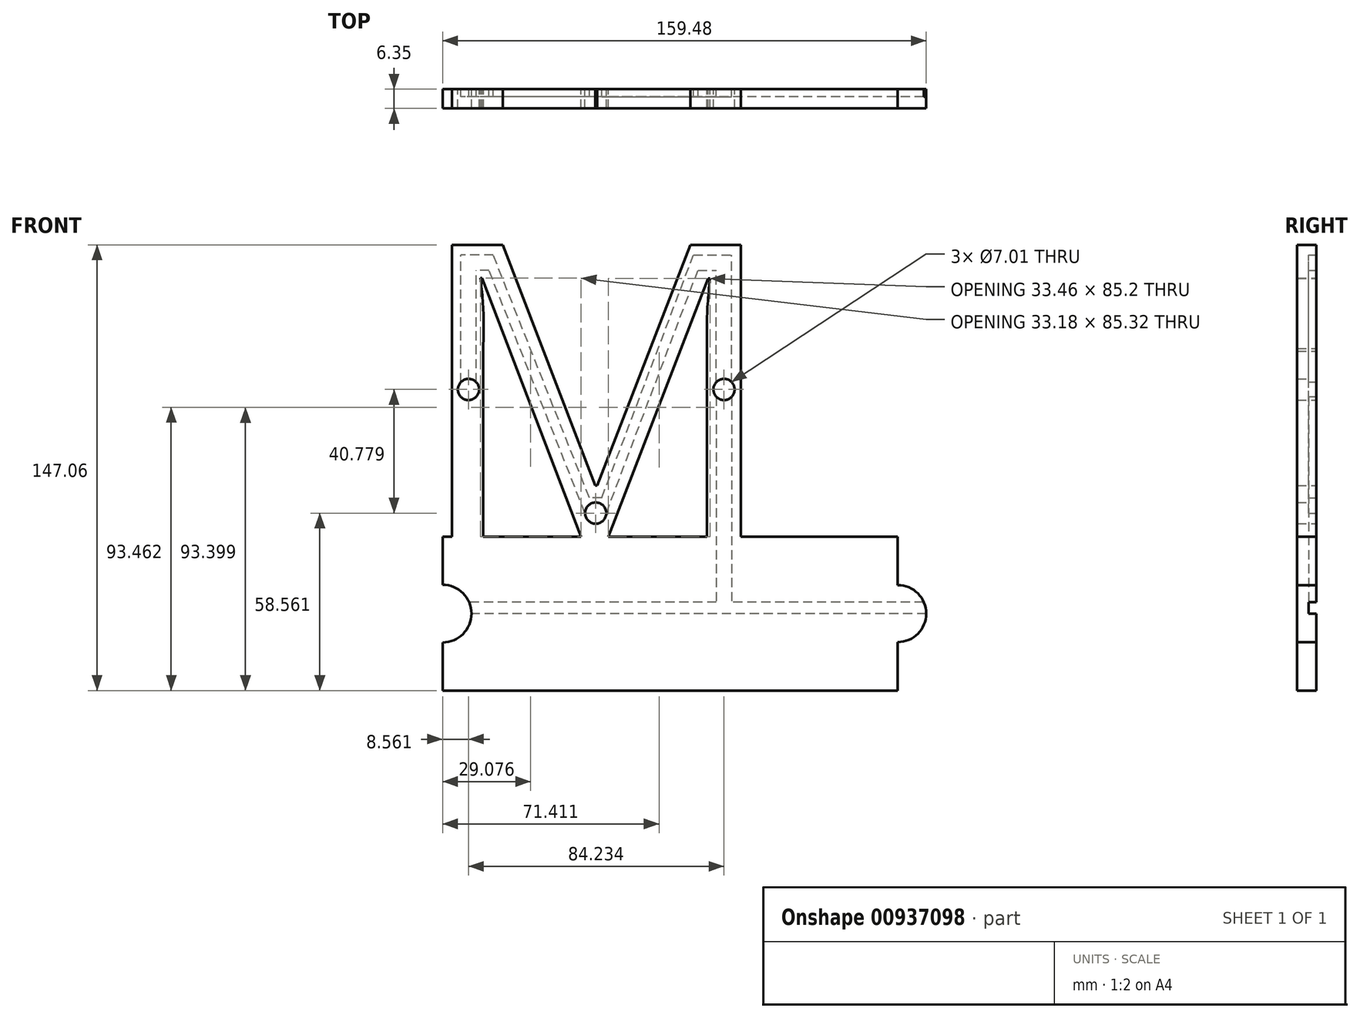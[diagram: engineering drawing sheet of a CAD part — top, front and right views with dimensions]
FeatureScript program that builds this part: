
annotation { "Feature Type Name" : "Feature", "Feature Type Description" : "" }
export const myFeature = defineFeature(function(context is Context, id is Id, definition is map)
    precondition{}
    {
        {
            var Q0;
            Q0=qCreatedBy(makeId("Front.planeOp"),FACE);
            var sketch = newSketch(context, id + "F0", { "sketchPlane" : qUnion([Q0])});
            skText(sketch, "E0", { "text": "M", "fontName": "OpenSans-Regular.ttf"});
            const initialGuessF0  = {"E0": [-0.05865, -0.04854, 1, 0, 0.09708]};
            skSetInitialGuess(sketch, initialGuessF0);
            skSolve(sketch);
        }
        {
            var Q0;
            Q0=qCreatedBy(makeId("Front.planeOp"),FACE);
            var sketch = newSketch(context, id + "F1", { "sketchPlane" : qUnion([Q0])});
            skLineSegment(sketch, "E1.0.0", {"start": v(-2.82, -48.54) * mm, "end": v(6.2, -48.54) * mm});
            skLineSegment(sketch, "E1.0.1", {"start": v(6.2, -48.54) * mm, "end": v(39.12, 36.66) * mm});
            skLineSegment(sketch, "E1.0.2", {"start": v(39.12, 36.66) * mm, "end": v(39.65, 36.66) * mm});
            skFitSpline(sketch, "E1.0.3", {"points": [v(39.65, 36.66) * mm, v(38.72, 24.14) * mm, v(38.72, 13.48) * mm]});
            skLineSegment(sketch, "E1.0.4", {"start": v(38.72, 13.48) * mm, "end": v(38.72, -48.54) * mm});
            skLineSegment(sketch, "E1.0.5", {"start": v(38.72, -48.54) * mm, "end": v(49.9, -48.54) * mm});
            skLineSegment(sketch, "E1.0.6", {"start": v(49.9, -48.54) * mm, "end": v(49.9, 47.72) * mm});
            skLineSegment(sketch, "E1.0.7", {"start": v(49.9, 47.72) * mm, "end": v(33.18, 47.72) * mm});
            skLineSegment(sketch, "E1.0.8", {"start": v(33.18, 47.72) * mm, "end": v(2.44, -31.69) * mm});
            skLineSegment(sketch, "E1.0.9", {"start": v(2.44, -31.69) * mm, "end": v(1.92, -31.69) * mm});
            skLineSegment(sketch, "E1.0.10", {"start": v(1.92, -31.69) * mm, "end": v(-28.57, 47.72) * mm});
            skLineSegment(sketch, "E1.0.11", {"start": v(-28.57, 47.72) * mm, "end": v(-45.42, 47.72) * mm});
            skLineSegment(sketch, "E1.0.12", {"start": v(-45.42, 47.72) * mm, "end": v(-45.42, -48.54) * mm});
            skLineSegment(sketch, "E1.0.13", {"start": v(-45.42, -48.54) * mm, "end": v(-35.08, -48.54) * mm});
            skLineSegment(sketch, "E1.0.14", {"start": v(-35.08, -48.54) * mm, "end": v(-35.08, 12.68) * mm});
            skFitSpline(sketch, "E1.0.15", {"points": [v(-35.08, 12.68) * mm, v(-35.08, 26.65) * mm, v(-36, 36.78) * mm]});
            skLineSegment(sketch, "E1.0.16", {"start": v(-36, 36.78) * mm, "end": v(-35.48, 36.78) * mm});
            skLineSegment(sketch, "E1.0.17", {"start": v(-35.48, 36.78) * mm, "end": v(-2.82, -48.54) * mm});
            skLineSegment(sketch, "E2.bottom", {"start": v(-48.5, -48.54) * mm, "end": v(101.6, -48.54) * mm});
            skLineSegment(sketch, "E2.top", {"start": v(-48.5, -99.34) * mm, "end": v(101.6, -99.34) * mm});
            skLineSegment(sketch, "E2.left", {"start": v(-48.5, -48.54) * mm, "end": v(-48.5, -64.41) * mm});
            skLineSegment(sketch, "E2.right", {"start": v(101.6, -48.54) * mm, "end": v(101.6, -64.54) * mm});
            skArc(sketch, "E3", {"start": v(-48.5, -83.46) * mm, "mid": v(-38.97, -73.94) * mm, "end": v(-48.5, -64.41) * mm});
            skLineSegment(sketch, "E4.trimOffspring", {"start": v(-48.5, -83.46) * mm, "end": v(-48.5, -99.34) * mm});
            skArc(sketch, "E5", {"start": v(101.6, -83.34) * mm, "mid": v(111, -73.94) * mm, "end": v(101.6, -64.54) * mm});
            skLineSegment(sketch, "E6.trimOffspring", {"start": v(101.6, -83.34) * mm, "end": v(101.6, -99.34) * mm});
            skCircle(sketch, "E7", {"center": v(2, -40.78) * mm, "radius": 3.5 * mm});
            skCircle(sketch, "E8", {"center": v(44.3, 0) * mm, "radius": 3.5 * mm});
            skCircle(sketch, "E9", {"center": v(-39.93, 0) * mm, "radius": 3.5 * mm});
            skSolve(sketch);
        }
        {
            var Q0;
            Q0 = qSketchRegion(id + "F1", true);
            extrude(context, id + "F2", {"entities" : qUnion([Q0]), "depth" : 6.35 * mm, "offsetDistance" : 25.4 * mm});
        }
        {
            var Q0;
            Q0=makeQuery(id+"F1.imprint","IMPRINT",FACE,{"disambiguationData":[TD([[makeQuery(id+"F1.imprint","IMPRINT",EDGE,{"derivedFrom":sQuery(id+"F1.wireOp",EDGE,"E2.top")}),1.0]])]});
            var sketch = newSketch(context, id + "F3", { "sketchPlane" : qUnion([Q0])});
            skCircle(sketch, "E10.0", {"center": v(44.3, 0) * mm, "radius": 3.5 * mm});
            skCircle(sketch, "E11.0", {"center": v(2, -40.78) * mm, "radius": 3.5 * mm});
            skCircle(sketch, "E12.0", {"center": v(-39.93, 0) * mm, "radius": 3.5 * mm});
            skLineSegment(sketch, "E13", {"start": v(44.3, 0) * mm, "end": v(44.3, 39.32) * mm, "construction": true});
            skLineSegment(sketch, "E14", {"start": v(-39.93, 0) * mm, "end": v(-39.93, 42.2) * mm, "construction": true});
            skLineSegment(sketch, "E15", {"start": v(5.5, -40.78) * mm, "end": v(35.73, 39.32) * mm});
            skLineSegment(sketch, "E16", {"start": v(35.73, 39.32) * mm, "end": v(41.77, 39.32) * mm});
            skLineSegment(sketch, "E17", {"start": v(-1.5, -40.78) * mm, "end": v(-33.17, 39.32) * mm});
            skLineSegment(sketch, "E18", {"start": v(44.3, 0) * mm, "end": v(44.3, -70.13) * mm});
            skPoint(sketch, "E19.0", {"position": v(111, -73.94) * mm});
            skLineSegment(sketch, "E20", {"start": v(111, -73.94) * mm, "end": v(-47.83, -73.94) * mm});
            skLineSegment(sketch, "E21.0", {"start": v(41.77, 0) * mm, "end": v(41.77, -70.13) * mm});
            skLineSegment(sketch, "E21.1", {"start": v(41.77, 0) * mm, "end": v(41.77, 39.32) * mm});
            skLineSegment(sketch, "E22.0", {"start": v(46.85, 0) * mm, "end": v(46.85, 44.4) * mm});
            skLineSegment(sketch, "E22.1", {"start": v(46.85, 0) * mm, "end": v(46.85, -70.13) * mm});
            skLineSegment(sketch, "E23.0", {"start": v(-37.39, 0) * mm, "end": v(-37.39, 39.32) * mm});
            skLineSegment(sketch, "E24.0", {"start": v(-42.47, 0) * mm, "end": v(-42.47, 44.4) * mm});
            skLineSegment(sketch, "E25.0", {"start": v(34.25, 44.4) * mm, "end": v(46.85, 44.4) * mm});
            skLineSegment(sketch, "E26", {"start": v(-33.17, 39.32) * mm, "end": v(-37.39, 39.32) * mm});
            skLineSegment(sketch, "E27.0", {"start": v(-31.76, 44.4) * mm, "end": v(-42.47, 44.4) * mm});
            skLineSegment(sketch, "E28", {"start": v(5.5, -40.78) * mm, "end": v(-1.5, -40.78) * mm});
            skLineSegment(sketch, "E29.0", {"start": v(4.03, -35.7) * mm, "end": v(-0.1, -35.7) * mm});
            skLineSegment(sketch, "E30.trimOffspring", {"start": v(4.03, -35.7) * mm, "end": v(34.25, 44.4) * mm});
            skLineSegment(sketch, "E31.trimOffspring", {"start": v(-0.1, -35.7) * mm, "end": v(-31.76, 44.4) * mm});
            skLineSegment(sketch, "E32", {"start": v(-37.39, 0) * mm, "end": v(-42.47, 0) * mm});
            skLineSegment(sketch, "E33.0", {"start": v(111, -70.13) * mm, "end": v(46.85, -70.13) * mm});
            skLineSegment(sketch, "E34.0", {"start": v(111, -77.75) * mm, "end": v(-47.83, -77.75) * mm});
            skLineSegment(sketch, "E35", {"start": v(111, -70.13) * mm, "end": v(111, -77.75) * mm});
            skLineSegment(sketch, "E36", {"start": v(-47.83, -70.13) * mm, "end": v(-47.83, -77.75) * mm});
            skLineSegment(sketch, "E37.trimOffspring", {"start": v(41.77, -70.13) * mm, "end": v(-47.83, -70.13) * mm});
            skSolve(sketch);
        }
        {
            var Q0;
            {var subQ5=sQuery(id+"F3.wireOp",EDGE,"E15");Q0=makeQuery(id+"F3.imprint","IMPRINT",FACE,{"disambiguationData":[TD([[makeQuery(id+"F3.imprint","IMPRINT",EDGE,{"derivedFrom":subQ5}),1.0]])]});}
            var Q1;
            {var subQ0=sQuery(id+"F3.wireOp",EDGE,"E33.0");var subQ1=sQuery(id+"F3.wireOp",EDGE,"E22.1");var subQ2=makeQuery(id+"F3.imprint","INTERSECT",VERTEX,{"derivedFrom":[subQ1,subQ0]});Q1=makeQuery(id+"F3.imprint","IMPRINT",FACE,{"disambiguationData":[TD([[makeQuery(id+"F3.imprint","IMPRINT",EDGE,{"disambiguationData":[TD([[subQ2,1.0]])],"derivedFrom":subQ0}),1.0]])]});}
            var Q2;
            {var subQ0=sQuery(id+"F3.wireOp",EDGE,"E21.0");var subQ1=sQuery(id+"F3.wireOp",EDGE,"E10.0");var subQ2=makeQuery(id+"F3.imprint","INTERSECT",VERTEX,{"derivedFrom":[subQ1,subQ0]});Q2=makeQuery(id+"F3.imprint","IMPRINT",FACE,{"disambiguationData":[TD([[makeQuery(id+"F3.imprint","IMPRINT",EDGE,{"disambiguationData":[TD([[subQ2,-1.0]])],"derivedFrom":subQ1}),-1.0]])]});}
            var Q3;
            {var subQ0=sQuery(id+"F3.wireOp",EDGE,"E18");var subQ1=sQuery(id+"F3.wireOp",EDGE,"E10.0");var subQ2=makeQuery(id+"F3.imprint","INTERSECT",VERTEX,{"derivedFrom":[subQ1,subQ0]});Q3=makeQuery(id+"F3.imprint","IMPRINT",FACE,{"disambiguationData":[TD([[makeQuery(id+"F3.imprint","IMPRINT",EDGE,{"disambiguationData":[TD([[subQ2,-1.0]])],"derivedFrom":subQ1}),-1.0]])]});}
            extrude(context, id + "F4", {"entities" : qUnion([Q0, Q1, Q2, Q3]), "operationType" : NewBodyOperationType.REMOVE, "depth" : 2.54 * mm, "offsetDistance" : 25.4 * mm});
        }
    });
